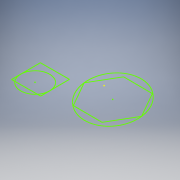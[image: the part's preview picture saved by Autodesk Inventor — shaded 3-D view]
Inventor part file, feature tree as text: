
AUTODESK INVENTOR PART (.ipt)
format: ipt  version: 2018 (Build 220112000, 112)  size: 90,624 bytes
history: native  units: in
note: dims shown in document units (in); Inventor stores cm internally (conversion verified against a paired STEP export)
features: sketch x1
ambient origin geometry x8: Origin, YZ Plane, XZ Plane, XY Plane, X Axis, Y Axis, Z Axis, Center Point
feature tree (1):
  sketch  "Sketch1"
